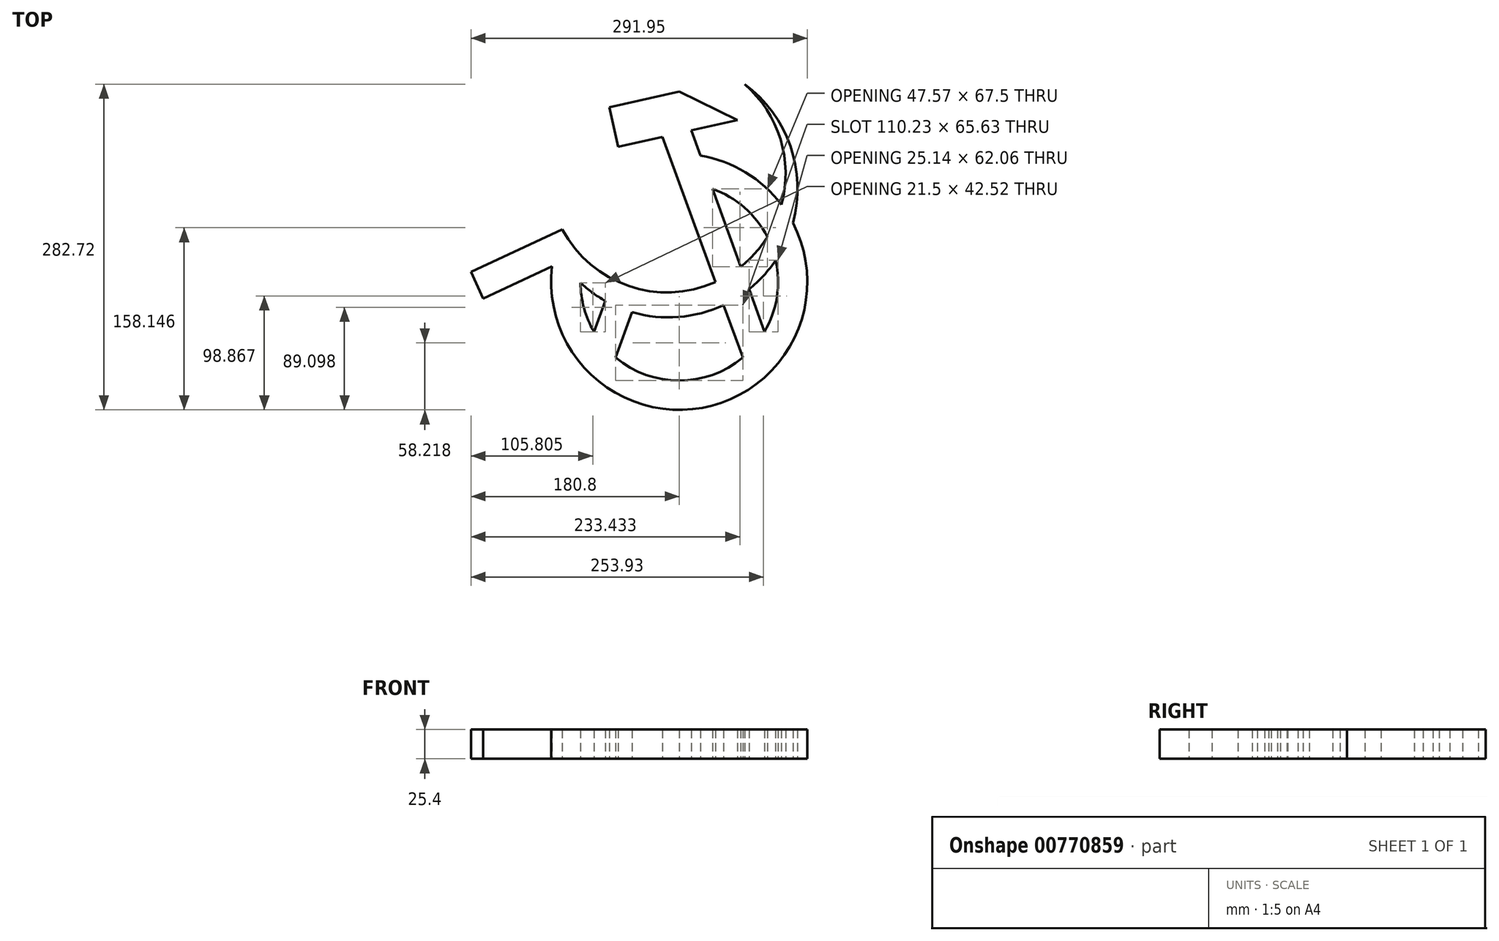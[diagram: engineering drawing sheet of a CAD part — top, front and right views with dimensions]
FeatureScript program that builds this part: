
annotation { "Feature Type Name" : "Feature", "Feature Type Description" : "" }
export const myFeature = defineFeature(function(context is Context, id is Id, definition is map)
    precondition{}
    {
        {
            var Q0;
            Q0=qCreatedBy(makeId("Top.planeOp"),FACE);
            var sketch = newSketch(context, id + "F0", { "sketchPlane" : qUnion([Q0])});
            skCircle(sketch, "E0", {"center": v(0, 0) * mm, "radius": 111.15 * mm});
            skCircle(sketch, "E1", {"center": v(0, 0) * mm, "radius": 85.75 * mm});
            skLineSegment(sketch, "E2", {"start": v(-55.12, -65.69) * mm, "end": v(0, 85.75) * mm});
            skLineSegment(sketch, "E3", {"start": v(0, 85.75) * mm, "end": v(55.12, -65.69) * mm});
            skLineSegment(sketch, "E4", {"start": v(-74, -43.31) * mm, "end": v(-28.85, 80.75) * mm});
            skLineSegment(sketch, "E5", {"start": v(28.85, 80.75) * mm, "end": v(74, -43.31) * mm});
            skLineSegment(sketch, "E6", {"start": v(-101.46, 45.37) * mm, "end": v(-180.8, 8.65) * mm});
            skLineSegment(sketch, "E7", {"start": v(-180.8, 8.65) * mm, "end": v(-170.13, -14.4) * mm});
            skLineSegment(sketch, "E8", {"start": v(-170.13, -14.4) * mm, "end": v(-101.46, 17.38) * mm});
            skArc(sketch, "E9", {"start": v(-101.46, 45.37) * mm, "mid": v(53.53, 13.33) * mm, "end": v(56.79, 171.57) * mm});
            skArc(sketch, "E10", {"start": v(-101.46, 17.38) * mm, "mid": v(68.82, 0.92) * mm, "end": v(56.79, 171.57) * mm});
            skLineSegment(sketch, "E11", {"start": v(-60.72, 151.58) * mm, "end": v(-53.03, 117.26) * mm});
            skLineSegment(sketch, "E12", {"start": v(-53.03, 117.26) * mm, "end": v(50.53, 140.46) * mm});
            skLineSegment(sketch, "E13", {"start": v(50.53, 140.46) * mm, "end": v(0, 165.18) * mm});
            skLineSegment(sketch, "E14", {"start": v(0, 165.18) * mm, "end": v(-60.72, 151.58) * mm});
            skLineSegment(sketch, "E15", {"start": v(0, 85.75) * mm, "end": v(-14.6, 125.87) * mm});
            skLineSegment(sketch, "E16", {"start": v(28.85, 80.75) * mm, "end": v(10.39, 131.47) * mm});
            skSolve(sketch);
        }
        {
            var Q0;
            {var subQ4=sQuery(id+"F0.wireOp",EDGE,"E11");Q0=makeQuery(id+"F0.imprint","IMPRINT",FACE,{"disambiguationData":[TD([[makeQuery(id+"F0.imprint","IMPRINT",EDGE,{"derivedFrom":subQ4}),1.0]])]});}
            var Q1;
            {var subQ0=sQuery(id+"F0.wireOp",EDGE,"E16");var subQ1=sQuery(id+"F0.wireOp",EDGE,"E0");var subQ2=makeQuery(id+"F0.imprint","INTERSECT",VERTEX,{"derivedFrom":[subQ1,subQ0]});Q1=makeQuery(id+"F0.imprint","IMPRINT",FACE,{"disambiguationData":[TD([[makeQuery(id+"F0.imprint","IMPRINT",EDGE,{"disambiguationData":[TD([[subQ2,-1.0]])],"derivedFrom":subQ1}),-1.0]])]});}
            var Q2;
            {var subQ0=sQuery(id+"F0.wireOp",EDGE,"E16");var subQ1=sQuery(id+"F0.wireOp",EDGE,"E0");var subQ2=makeQuery(id+"F0.imprint","INTERSECT",VERTEX,{"derivedFrom":[subQ1,subQ0]});Q2=makeQuery(id+"F0.imprint","IMPRINT",FACE,{"disambiguationData":[TD([[makeQuery(id+"F0.imprint","IMPRINT",EDGE,{"disambiguationData":[TD([[subQ2,-1.0]])],"derivedFrom":subQ1}),1.0]])]});}
            var Q3;
            {var subQ0=sQuery(id+"F0.wireOp",EDGE,"E3");var subQ5=sQuery(id+"F0.wireOp",EDGE,"E9");var subQ6=makeQuery(id+"F0.imprint","INTERSECT",VERTEX,{"derivedFrom":[subQ0,subQ5]});Q3=makeQuery(id+"F0.imprint","IMPRINT",FACE,{"disambiguationData":[TD([[makeQuery(id+"F0.imprint","IMPRINT",EDGE,{"disambiguationData":[TD([[subQ6,-1.0]])],"derivedFrom":subQ5}),1.0]])]});}
            var Q4;
            {var subQ0=sQuery(id+"F0.wireOp",EDGE,"E9");var subQ1=sQuery(id+"F0.wireOp",EDGE,"E3");var subQ2=makeQuery(id+"F0.imprint","INTERSECT",VERTEX,{"derivedFrom":[subQ1,subQ0]});Q4=makeQuery(id+"F0.imprint","IMPRINT",FACE,{"disambiguationData":[TD([[makeQuery(id+"F0.imprint","IMPRINT",EDGE,{"disambiguationData":[TD([[subQ2,-1.0]])],"derivedFrom":subQ1}),1.0]])]});}
            var Q5;
            {var subQ0=sQuery(id+"F0.wireOp",EDGE,"E3");var subQ1=sQuery(id+"F0.wireOp",EDGE,"E1");var subQ2=makeQuery(id+"F0.imprint","INTERSECT",VERTEX,{"derivedFrom":[subQ1,subQ0]});Q5=makeQuery(id+"F0.imprint","IMPRINT",FACE,{"disambiguationData":[TD([[makeQuery(id+"F0.imprint","IMPRINT",EDGE,{"disambiguationData":[TD([[subQ2,-1.0]])],"derivedFrom":subQ1}),1.0]])]});}
            var Q6;
            {var subQ3=sQuery(id+"F0.wireOp",EDGE,"E10");var subQ4=sQuery(id+"F0.wireOp",EDGE,"E0");var subQ5=makeQuery(id+"F0.imprint","INTERSECT",VERTEX,{"derivedFrom":[subQ4,subQ3]});Q6=makeQuery(id+"F0.imprint","IMPRINT",FACE,{"disambiguationData":[TD([[makeQuery(id+"F0.imprint","IMPRINT",EDGE,{"disambiguationData":[TD([[subQ5,1.0]])],"derivedFrom":subQ4}),1.0]])]});}
            var Q7;
            {var subQ0=sQuery(id+"F0.wireOp",EDGE,"E9");var subQ1=sQuery(id+"F0.wireOp",EDGE,"E0");var subQ2=makeQuery(id+"F0.imprint","INTERSECT",VERTEX,{"derivedFrom":[subQ1,subQ0]});Q7=makeQuery(id+"F0.imprint","IMPRINT",FACE,{"disambiguationData":[TD([[makeQuery(id+"F0.imprint","IMPRINT",EDGE,{"disambiguationData":[TD([[subQ2,1.0]])],"derivedFrom":subQ1}),1.0]])]});}
            var Q8;
            {var subQ0=sQuery(id+"F0.wireOp",EDGE,"E9");var subQ1=sQuery(id+"F0.wireOp",EDGE,"E0");var subQ2=makeQuery(id+"F0.imprint","INTERSECT",VERTEX,{"derivedFrom":[subQ1,subQ0]});Q8=makeQuery(id+"F0.imprint","IMPRINT",FACE,{"disambiguationData":[TD([[makeQuery(id+"F0.imprint","IMPRINT",EDGE,{"disambiguationData":[TD([[subQ2,1.0]])],"derivedFrom":subQ1}),-1.0]])]});}
            var Q9;
            {var subQ0=sQuery(id+"F0.wireOp",EDGE,"E9");var subQ1=sQuery(id+"F0.wireOp",EDGE,"E0");var subQ2=makeQuery(id+"F0.imprint","INTERSECT",VERTEX,{"derivedFrom":[subQ1,subQ0]});Q9=makeQuery(id+"F0.imprint","IMPRINT",FACE,{"disambiguationData":[TD([[makeQuery(id+"F0.imprint","IMPRINT",EDGE,{"disambiguationData":[TD([[subQ2,-1.0]])],"derivedFrom":subQ1}),1.0]])]});}
            var Q10;
            {var subQ0=sQuery(id+"F0.wireOp",EDGE,"E1");var subQ1=makeQuery(id+"F0.imprint","INTERSECT",VERTEX,{"disambiguationData":[OD(1.0)],"derivedFrom":[subQ0,sQuery(id+"F0.wireOp",EDGE,"E4")]});Q10=makeQuery(id+"F0.imprint","IMPRINT",FACE,{"disambiguationData":[TD([[makeQuery(id+"F0.imprint","IMPRINT",EDGE,{"disambiguationData":[TD([[subQ1,-1.0]])],"derivedFrom":subQ0}),-1.0]])]});}
            var Q11;
            {var subQ1=sQuery(id+"F0.wireOp",EDGE,"E1");var subQ3=sQuery(id+"F0.wireOp",EDGE,"E4");var subQ4=makeQuery(id+"F0.imprint","INTERSECT",VERTEX,{"disambiguationData":[OD(1.0)],"derivedFrom":[subQ1,subQ3]});Q11=makeQuery(id+"F0.imprint","IMPRINT",FACE,{"disambiguationData":[TD([[makeQuery(id+"F0.imprint","IMPRINT",EDGE,{"disambiguationData":[TD([[subQ4,1.0]])],"derivedFrom":subQ3}),-1.0]])]});}
            var Q12;
            {var subQ0=sQuery(id+"F0.wireOp",EDGE,"E10");var subQ1=sQuery(id+"F0.wireOp",EDGE,"E2");var subQ2=makeQuery(id+"F0.imprint","INTERSECT",VERTEX,{"derivedFrom":[subQ1,subQ0]});Q12=makeQuery(id+"F0.imprint","IMPRINT",FACE,{"disambiguationData":[TD([[makeQuery(id+"F0.imprint","IMPRINT",EDGE,{"disambiguationData":[TD([[subQ2,-1.0]])],"derivedFrom":subQ1}),-1.0]])]});}
            var Q13;
            {var subQ0=sQuery(id+"F0.wireOp",EDGE,"E9");var subQ1=sQuery(id+"F0.wireOp",EDGE,"E1");var subQ2=makeQuery(id+"F0.imprint","INTERSECT",VERTEX,{"disambiguationData":[OD(0.0)],"derivedFrom":[subQ1,subQ0]});Q13=makeQuery(id+"F0.imprint","IMPRINT",FACE,{"disambiguationData":[TD([[makeQuery(id+"F0.imprint","IMPRINT",EDGE,{"disambiguationData":[TD([[subQ2,1.0]])],"derivedFrom":subQ1}),1.0]])]});}
            var Q14;
            {var subQ0=sQuery(id+"F0.wireOp",EDGE,"E10");var subQ1=sQuery(id+"F0.wireOp",EDGE,"E2");var subQ2=makeQuery(id+"F0.imprint","INTERSECT",VERTEX,{"derivedFrom":[subQ1,subQ0]});Q14=makeQuery(id+"F0.imprint","IMPRINT",FACE,{"disambiguationData":[TD([[makeQuery(id+"F0.imprint","IMPRINT",EDGE,{"disambiguationData":[TD([[subQ2,-1.0]])],"derivedFrom":subQ1}),1.0]])]});}
            var Q15;
            {var subQ0=sQuery(id+"F0.wireOp",EDGE,"E2");var subQ1=sQuery(id+"F0.wireOp",EDGE,"E1");var subQ2=makeQuery(id+"F0.imprint","INTERSECT",VERTEX,{"derivedFrom":[subQ1,subQ0]});Q15=makeQuery(id+"F0.imprint","IMPRINT",FACE,{"disambiguationData":[TD([[makeQuery(id+"F0.imprint","IMPRINT",EDGE,{"disambiguationData":[TD([[subQ2,1.0]])],"derivedFrom":subQ1}),1.0]])]});}
            var Q16;
            {var subQ0=sQuery(id+"F0.wireOp",EDGE,"E9");var subQ1=sQuery(id+"F0.wireOp",EDGE,"E1");var subQ2=makeQuery(id+"F0.imprint","INTERSECT",VERTEX,{"disambiguationData":[OD(1.0)],"derivedFrom":[subQ1,subQ0]});Q16=makeQuery(id+"F0.imprint","IMPRINT",FACE,{"disambiguationData":[TD([[makeQuery(id+"F0.imprint","IMPRINT",EDGE,{"disambiguationData":[TD([[subQ2,-1.0]])],"derivedFrom":subQ1}),1.0]])]});}
            var Q17;
            {var subQ0=sQuery(id+"F0.wireOp",EDGE,"E6");Q17=makeQuery(id+"F0.imprint","IMPRINT",FACE,{"disambiguationData":[TD([[makeQuery(id+"F0.imprint","IMPRINT",EDGE,{"derivedFrom":subQ0}),1.0]])]});}
            var Q18;
            {var subQ0=sQuery(id+"F0.wireOp",EDGE,"E9");var subQ3=sQuery(id+"F0.wireOp",EDGE,"E1");var subQ4=makeQuery(id+"F0.imprint","INTERSECT",VERTEX,{"disambiguationData":[OD(1.0)],"derivedFrom":[subQ3,subQ0]});Q18=makeQuery(id+"F0.imprint","IMPRINT",FACE,{"disambiguationData":[TD([[makeQuery(id+"F0.imprint","IMPRINT",EDGE,{"disambiguationData":[TD([[subQ4,-1.0]])],"derivedFrom":subQ3}),-1.0]])]});}
            var Q19;
            Q19=sQuery(id+"F0.wireOp",EDGE,"E2");
            var Q20;
            Q20=sQuery(id+"F0.wireOp",EDGE,"E11");
            var Q21;
            Q21=sQuery(id+"F0.wireOp",EDGE,"E0");
            var Q22;
            Q22=sQuery(id+"F0.wireOp",EDGE,"E1");
            var Q23;
            Q23=sQuery(id+"F0.wireOp",EDGE,"E16");
            var Q24;
            Q24=sQuery(id+"F0.wireOp",EDGE,"E12");
            var Q25;
            Q25=sQuery(id+"F0.wireOp",EDGE,"E10");
            var Q26;
            Q26=sQuery(id+"F0.wireOp",EDGE,"E5");
            var Q27;
            Q27=sQuery(id+"F0.wireOp",EDGE,"E8");
            var Q28;
            Q28=sQuery(id+"F0.wireOp",EDGE,"E9");
            var Q29;
            Q29=sQuery(id+"F0.wireOp",EDGE,"E7");
            var Q30;
            Q30=sQuery(id+"F0.wireOp",EDGE,"E3");
            var Q31;
            Q31=sQuery(id+"F0.wireOp",EDGE,"E6");
            var Q32;
            Q32=sQuery(id+"F0.wireOp",EDGE,"E15");
            var Q33;
            Q33=sQuery(id+"F0.wireOp",EDGE,"E4");
            var Q34;
            Q34=sQuery(id+"F0.wireOp",EDGE,"E14");
            var Q35;
            Q35=sQuery(id+"F0.wireOp",EDGE,"E13");
            extrude(context, id + "F1", {"entities" : qUnion([Q0, Q1, Q2, Q3, Q4, Q5, Q6, Q7, Q8, Q9, Q10, Q11, Q12, Q13, Q14, Q15, Q16, Q17, Q18]), "surfaceEntities" : qUnion([Q19, Q20, Q21, Q22, Q23, Q24, Q25, Q26, Q27, Q28, Q29, Q30, Q31, Q32, Q33, Q34, Q35]), "depth" : 25.4 * mm, "offsetDistance" : 25.4 * mm});
        }
    });
